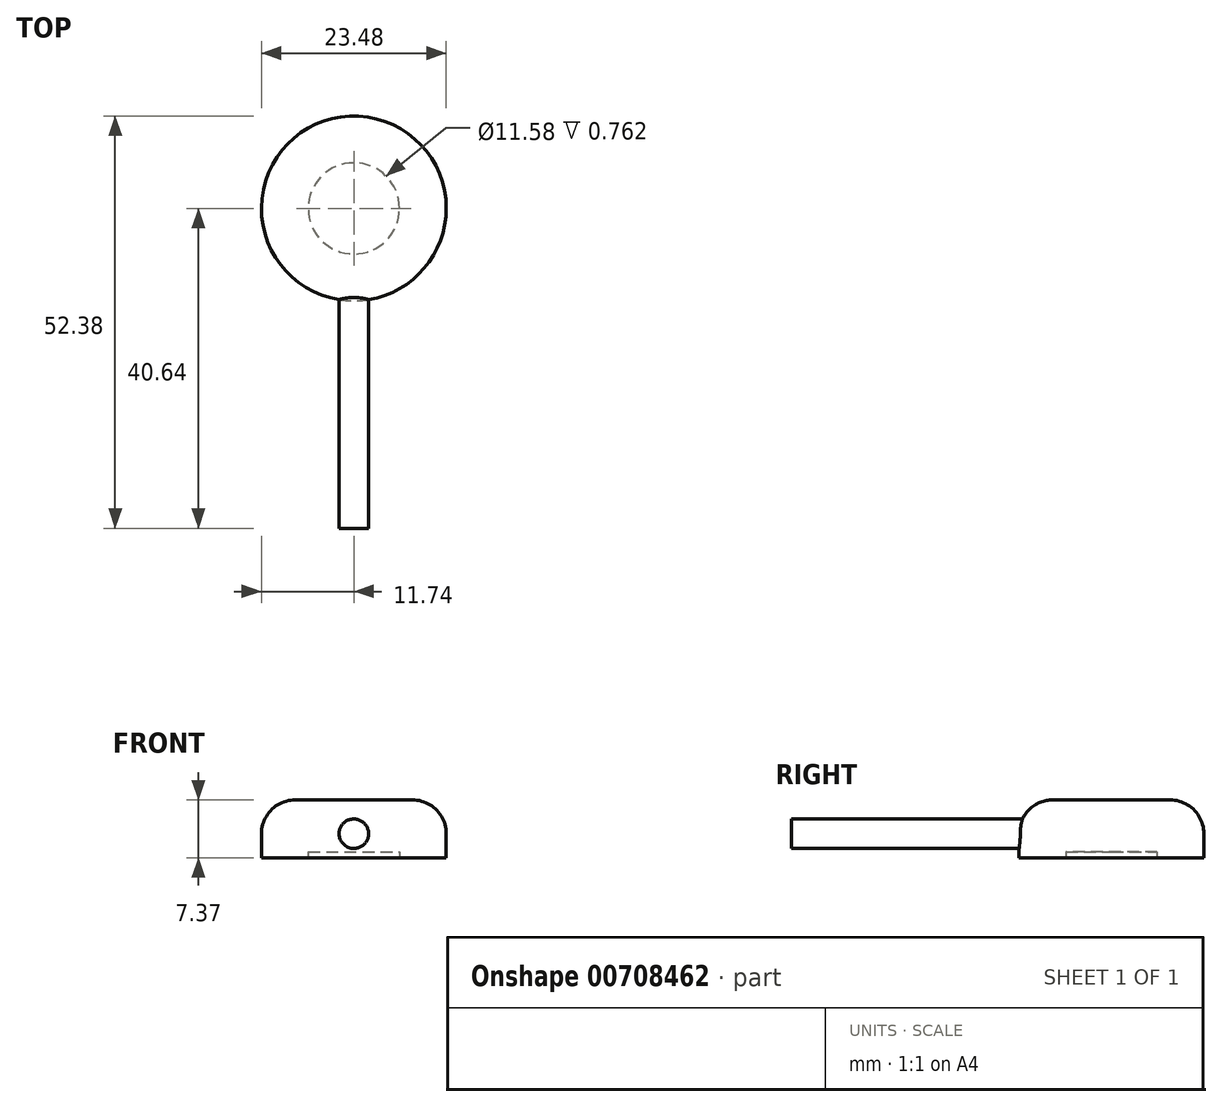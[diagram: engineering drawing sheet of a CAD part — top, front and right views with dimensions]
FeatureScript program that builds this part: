
annotation { "Feature Type Name" : "Feature", "Feature Type Description" : "" }
export const myFeature = defineFeature(function(context is Context, id is Id, definition is map)
    precondition{}
    {
        {
            var Q0;
            Q0=qCreatedBy(makeId("Top.planeOp"),FACE);
            var sketch = newSketch(context, id + "F0", { "sketchPlane" : qUnion([Q0])});
            skCircle(sketch, "E0", {"center": v(0, 0) * mm, "radius": 11.74 * mm});
            skSolve(sketch);
        }
        {
            var Q0;
            Q0=makeQuery(id+"F0.imprint","IMPRINT",FACE,{"disambiguationData":[TD([[makeQuery(id+"F0.imprint","IMPRINT",EDGE,{"derivedFrom":sQuery(id+"F0.wireOp",EDGE,"E0")}),1.0]])]});
            extrude(context, id + "F1", {"entities" : qUnion([Q0]), "depth" : 7.37 * mm, "offsetDistance" : 25.4 * mm});
        }
        {
            var Q0;
            Q0=makeQuery(id+"F1.opExtrude","CAP_EDGE",EDGE,{"disambiguationData":[OSD([sQuery(id+"F0.wireOp",EDGE,"E0")])],"isStart":false});
            fillet(context, id + "F2", {"entities" : qUnion([Q0]), "radius" : 4.3 * mm, "tangentPropagation" : true, "allowEdgeOverflow" : false});
        }
        {
            var Q0;
            Q0=makeQuery(id+"F1.opExtrude","CAP_FACE",FACE,{"disambiguationData":[OSD([sQuery(id+"F0.wireOp",EDGE,"E0")])],"isStart":true});
            var sketch = newSketch(context, id + "F3", { "sketchPlane" : qUnion([Q0])});
            skCircle(sketch, "E1", {"center": v(0, 0) * mm, "radius": 5.8 * mm});
            skSolve(sketch);
        }
        {
            var Q0;
            Q0=makeQuery(id+"F3.imprint","IMPRINT",FACE,{"disambiguationData":[TD([[makeQuery(id+"F3.imprint","IMPRINT",EDGE,{"derivedFrom":sQuery(id+"F3.wireOp",EDGE,"E1")}),1.0]])]});
            extrude(context, id + "F4", {"entities" : qUnion([Q0]), "operationType" : NewBodyOperationType.REMOVE, "oppositeDirection" : true, "depth" : 0.76 * mm, "offsetDistance" : 25.4 * mm});
        }
        {
            var Q0;
            Q0=qCreatedBy(makeId("Front.planeOp"),FACE);
            var sketch = newSketch(context, id + "F5", { "sketchPlane" : qUnion([Q0])});
            skCircle(sketch, "E2", {"center": v(0, 3.07) * mm, "radius": 1.88 * mm});
            skSolve(sketch);
        }
        {
            var Q0;
            Q0=qSketchRegion(id+"F5",true);
            extrude(context, id + "F6", {"entities" : qUnion([Q0]), "operationType" : NewBodyOperationType.ADD, "depth" : 40.64 * mm, "offsetDistance" : 25.4 * mm});
        }
    });
